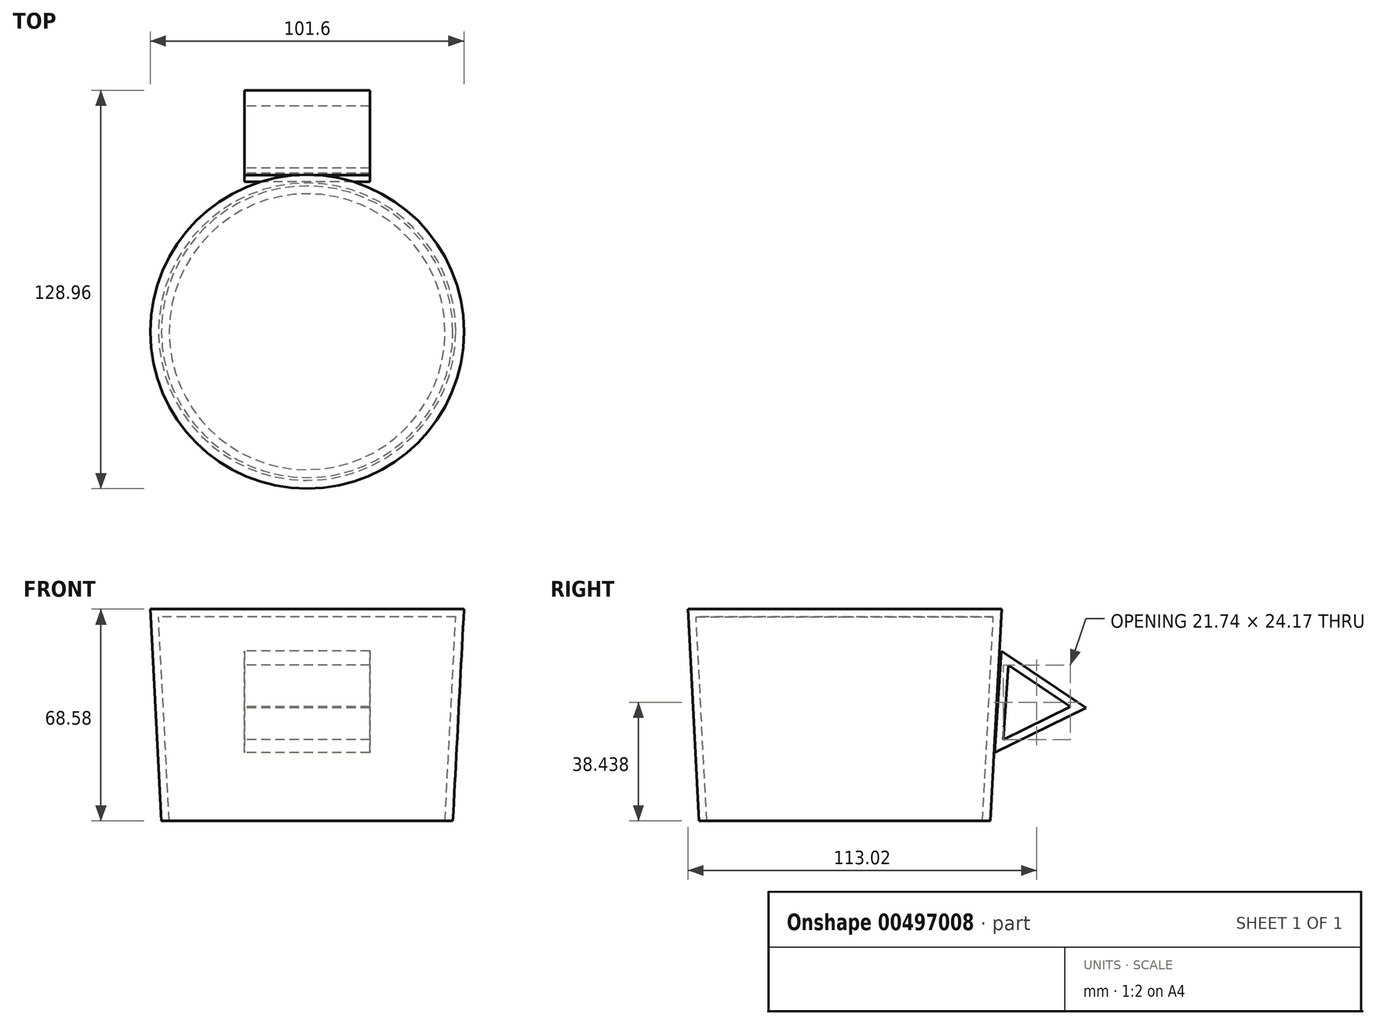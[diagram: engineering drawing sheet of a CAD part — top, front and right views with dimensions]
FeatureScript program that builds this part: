
annotation { "Feature Type Name" : "Feature", "Feature Type Description" : "" }
export const myFeature = defineFeature(function(context is Context, id is Id, definition is map)
    precondition{}
    {
        {
            var Q0;
            Q0=qCreatedBy(makeId("Top.planeOp"),FACE);
            var sketch = newSketch(context, id + "F0", { "sketchPlane" : qUnion([Q0])});
            skCircle(sketch, "E0", {"center": v(0, 0) * mm, "radius": 47.2 * mm});
            skSolve(sketch);
        }
        {
            var Q0;
            Q0=makeQuery(id+"F0.imprint","IMPRINT",FACE,{"disambiguationData":[TD([[makeQuery(id+"F0.imprint","IMPRINT",EDGE,{"derivedFrom":sQuery(id+"F0.wireOp",EDGE,"E0")}),1.0]])]});
            extrude(context, id + "F1", {"entities" : qUnion([Q0]), "depth" : 68.58 * mm, "hasDraft" : true, "draftAngle" : 3 * degree});
        }
        {
            var Q0;
            Q0=qCreatedBy(makeId("Right.planeOp"),FACE);
            var sketch = newSketch(context, id + "F2", { "sketchPlane" : qUnion([Q0])});
            skLineSegment(sketch, "E1", {"start": v(50.74, 55.08) * mm, "end": v(78.16, 36.68) * mm});
            skLineSegment(sketch, "E2", {"start": v(78.16, 36.68) * mm, "end": v(48.52, 22.14) * mm});
            skLineSegment(sketch, "E3", {"start": v(48.52, 22.14) * mm, "end": v(50.74, 55.08) * mm});
            skSolve(sketch);
        }
        {
            var Q0;
            Q0=makeQuery(id+"F2.imprint","IMPRINT",FACE,{"disambiguationData":[TD([[makeQuery(id+"F2.imprint","IMPRINT",EDGE,{"derivedFrom":sQuery(id+"F2.wireOp",EDGE,"E1")}),-1.0]])]});
            extrude(context, id + "F3", {"entities" : qUnion([Q0]), "endBound" : BoundingType.SYMMETRIC, "depth" : 40.64 * mm});
        }
        {
            var Q0;
            Q0=makeQuery(id+"F3.opExtrude","CAP_FACE",FACE,{"disambiguationData":[OSD([sQuery(id+"F2.wireOp",EDGE,"E1"),sQuery(id+"F2.wireOp",EDGE,"E2"),sQuery(id+"F2.wireOp",EDGE,"E3")])],"isStart":true});
            var Q1;
            Q1=makeQuery(id+"F3.opExtrude","CAP_FACE",FACE,{"disambiguationData":[OSD([sQuery(id+"F2.wireOp",EDGE,"E1"),sQuery(id+"F2.wireOp",EDGE,"E2"),sQuery(id+"F2.wireOp",EDGE,"E3")])],"isStart":false});
            var Q2;
            Q2=makeQuery(id+"F3.opExtrude","SWEPT_BODY",BODY,{"disambiguationData":[OSD([sQuery(id+"F2.wireOp",EDGE,"E1"),sQuery(id+"F2.wireOp",EDGE,"E2"),sQuery(id+"F2.wireOp",EDGE,"E3")])]});
            shell(context, id + "F4", {"entities" : qUnion([Q0, Q1]), "parts" : qUnion([Q2]), "thickness" : 2.54 * mm});
        }
        {
            var Q0;
            Q0=makeQuery(id+"F1.opExtrude","CAP_FACE",FACE,{"disambiguationData":[OSD([sQuery(id+"F0.wireOp",EDGE,"E0")])],"isStart":true});
            shell(context, id + "F5", {"entities" : qUnion([Q0]), "thickness" : 2.54 * mm});
        }
    });
